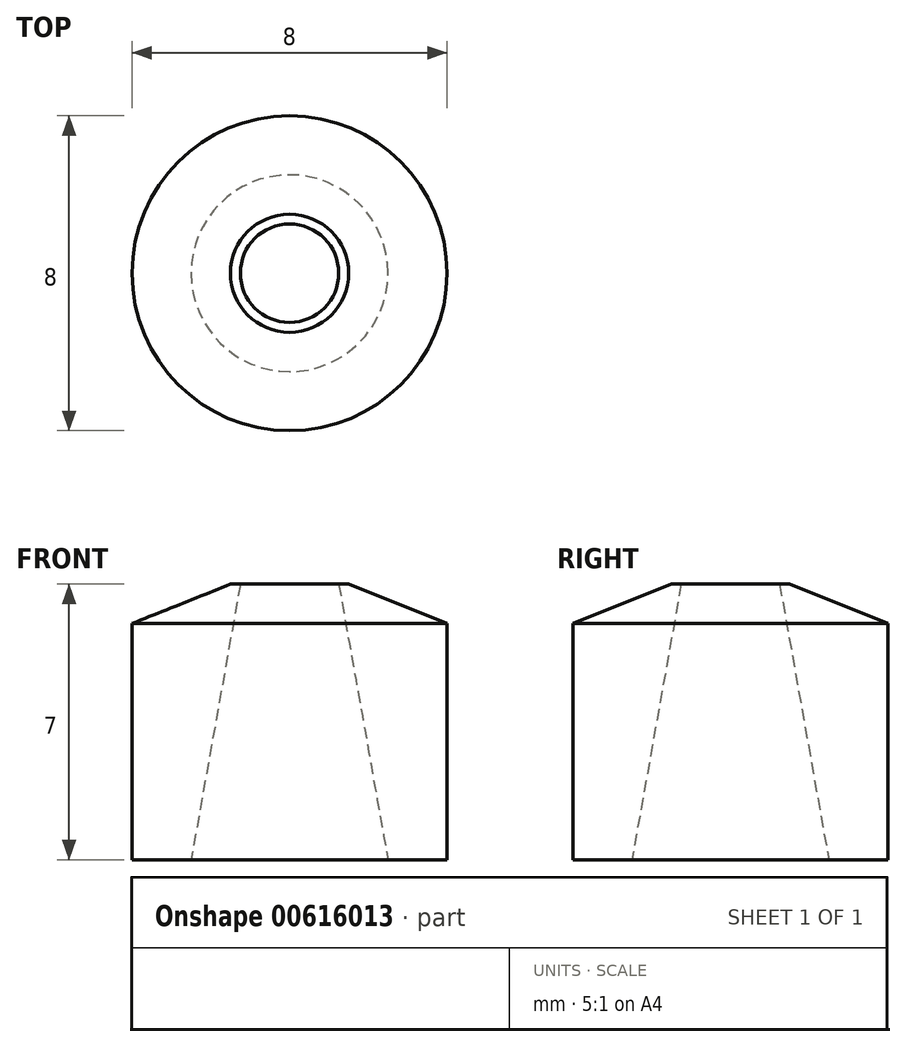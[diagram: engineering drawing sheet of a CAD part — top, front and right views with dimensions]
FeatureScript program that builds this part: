
annotation { "Feature Type Name" : "Feature", "Feature Type Description" : "" }
export const myFeature = defineFeature(function(context is Context, id is Id, definition is map)
    precondition{}
    {
        {
            var Q0;
            Q0=qCreatedBy(makeId("Right.planeOp"),FACE);
            var sketch = newSketch(context, id + "F0", { "sketchPlane" : qUnion([Q0])});
            skLineSegment(sketch, "E0", {"start": v(0, 0) * mm, "end": v(2.5, 0) * mm});
            skLineSegment(sketch, "E1", {"start": v(2.5, 0) * mm, "end": v(1.25, 7) * mm});
            skLineSegment(sketch, "E2", {"start": v(1.25, 7) * mm, "end": v(0, 7) * mm});
            skLineSegment(sketch, "E3", {"start": v(0, 7) * mm, "end": v(0, 0) * mm});
            skSolve(sketch);
        }
        {
            var Q0;
            Q0=qCreatedBy(makeId("Right.planeOp"),FACE);
            var sketch = newSketch(context, id + "F1", { "sketchPlane" : qUnion([Q0])});
            skLineSegment(sketch, "E4", {"start": v(0, 0) * mm, "end": v(4, 0) * mm});
            skLineSegment(sketch, "E5", {"start": v(4, 0) * mm, "end": v(4, 7) * mm});
            skLineSegment(sketch, "E6", {"start": v(4, 7) * mm, "end": v(0, 7) * mm});
            skLineSegment(sketch, "E7", {"start": v(0, 7) * mm, "end": v(0, 0) * mm});
            skSolve(sketch);
        }
        {
            var Q0;
            Q0=makeQuery(id+"F1.imprint","IMPRINT",FACE,{"disambiguationData":[TD([[makeQuery(id+"F1.imprint","IMPRINT",EDGE,{"derivedFrom":sQuery(id+"F1.wireOp",EDGE,"E4")}),1.0]])]});
            var Q1;
            Q1=sQuery(id+"F1.wireOp",EDGE,"E7");
            revolve(context, id + "F2", {"entities" : qUnion([Q0]), "axis" : qUnion([Q1]), "revolveType" : RevolveType.FULL});
        }
        {
            var Q0;
            Q0=makeQuery(id+"F0.imprint","IMPRINT",FACE,{"disambiguationData":[TD([[makeQuery(id+"F0.imprint","IMPRINT",EDGE,{"derivedFrom":sQuery(id+"F0.wireOp",EDGE,"E0")}),1.0]])]});
            var Q1;
            Q1=sQuery(id+"F0.wireOp",EDGE,"E3");
            revolve(context, id + "F3", {"entities" : qUnion([Q0]), "axis" : qUnion([Q1]), "revolveType" : RevolveType.FULL});
        }
        {
            var Q0;
            Q0=makeQuery(id+"F3.opRevolve","SWEPT_BODY",BODY,{"disambiguationData":[OSD([sQuery(id+"F0.wireOp",EDGE,"E0"),sQuery(id+"F0.wireOp",EDGE,"E1"),sQuery(id+"F0.wireOp",EDGE,"E2"),sQuery(id+"F0.wireOp",EDGE,"E3")])]});
            var Q1;
            Q1=makeQuery(id+"F2.opRevolve","SWEPT_BODY",BODY,{"disambiguationData":[OSD([sQuery(id+"F1.wireOp",EDGE,"E4"),sQuery(id+"F1.wireOp",EDGE,"E5"),sQuery(id+"F1.wireOp",EDGE,"E6"),sQuery(id+"F1.wireOp",EDGE,"E7")])]});
            booleanBodies(context, id + "F4", {"operationType" : BooleanOperationType.SUBTRACTION, "tools" : qUnion([Q0]), "targets" : qUnion([Q1])});
        }
        {
            var Q0;
            Q0=makeQuery(id+"F2.opRevolve","SWEPT_EDGE",EDGE,{"disambiguationData":[OSD([sQuery(id+"F1.wireOp",EDGE,"E5"),sQuery(id+"F1.wireOp",EDGE,"E6")])]});
            chamfer(context, id + "F5", {"entities" : qUnion([Q0]), "chamferType" : ChamferType.TWO_OFFSETS, "width1" : 2.5 * mm, "oppositeDirection" : false, "width2" : 1 * mm, "tangentPropagation" : true});
        }
    });
